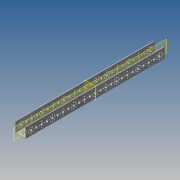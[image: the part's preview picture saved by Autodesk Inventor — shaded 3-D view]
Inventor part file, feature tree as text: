
AUTODESK INVENTOR PART (.ipt)
format: ipt  version: 2020 (Build 240168000, 168)  size: 620,032 bytes
history: native  units: in
note: dims shown in document units (in); Inventor stores cm internally (conversion verified against a paired STEP export)
features: other x216, plane x2, imported_body x1
ambient origin geometry x8: Origin, YZ Plane, XZ Plane, XY Plane, X Axis, Y Axis, Z Axis, Center Point
bodies: Body1 (feature_tree)
feature tree (219):
  other  "tetrix_739069_2012"
  other  "tetrix_739069_20121"
  other  "A_1"
  other  "A_78"
  other  "A_79"
  other  "A_80"
  other  "A_81"
  other  "A_82"
  other  "A_83"
  other  "A_84"
  other  "A_85"
  other  "A_27"
  other  "A_86"
  other  "A_87"
  other  "A_88"
  other  "A_89"
  other  "A_90"
  other  "A_91"
  other  "A_92"
  other  "A_93"
  other  "A_119"
  other  "A_120"
  other  "A_121"
  other  "A_122"
  other  "A_123"
  other  "A_124"
  other  "A_125"
  other  "A_126"
  other  "A_127"
  other  "A_149"
  other  "A_150"
  other  "A_151"
  other  "A_152"
  other  "A_153"
  other  "A_154"
  other  "A_155"
  other  "A_156"
  other  "A_157"
  other  "A_158"
  other  "A_159"
  other  "A_160"
  other  "A_161"
  other  "A_162"
  other  "A_163"
  other  "A_164"
  other  "A_165"
  other  "A_166"
  other  "Work Axis46"
  other  "Work Axis47"
  other  "Work Axis48"
  other  "Work Axis49"
  other  "Work Axis50"
  other  "Work Axis51"
  other  "Work Axis52"
  other  "Work Axis53"
  other  "Work Axis54"
  other  "Work Axis55"
  other  "Work Axis56"
  other  "Work Axis57"
  other  "Work Axis58"
  other  "Work Axis59"
  other  "Work Axis60"
  other  "Work Axis61"
  other  "Work Axis62"
  other  "Work Axis63"
  other  "A_18"
  other  "A_94"
  other  "A_95"
  other  "A_96"
  other  "A_97"
  other  "A_98"
  other  "A_99"
  other  "A_100"
  other  "A_101"
  other  "A_31"
  other  "A_102"
  other  "A_103"
  other  "A_104"
  other  "A_105"
  other  "A_106"
  other  "A_107"
  other  "A_108"
  other  "A_109"
  other  "A_128"
  other  "A_129"
  other  "A_130"
  other  "A_131"
  other  "A_132"
  other  "A_133"
  other  "A_134"
  other  "A_135"
  other  "A_136"
  other  "A_1283"
  other  "A_1284"
  other  "A_1285"
  other  "A_1286"
  other  "A_1287"
  other  "A_1288"
  other  "A_1289"
  other  "A_1290"
  other  "A_1291"
  other  "A_1292"
  other  "A_1293"
  other  "A_1294"
  other  "A_1295"
  other  "A_1296"
  other  "A_1297"
  other  "A_1298"
  other  "A_1299"
  other  "A_1300"
  other  "Work Axis109"
  other  "Work Axis110"
  other  "Work Axis111"
  other  "Work Axis112"
  other  "Work Axis113"
  other  "Work Axis114"
  other  "Work Axis115"
  other  "Work Axis116"
  other  "Work Axis117"
  other  "Work Axis118"
  other  "Work Axis119"
  other  "Work Axis120"
  other  "Work Axis121"
  other  "Work Axis122"
  other  "Work Axis123"
  other  "Work Axis124"
  other  "Work Axis125"
  other  "Work Axis126"
  other  "A_77"
  other  "A_110"
  other  "A_111"
  other  "A_112"
  other  "A_113"
  other  "A_139"
  other  "A_140"
  other  "A_141"
  other  "A_142"
  other  "A_143"
  other  "A_2421"
  other  "A_2422"
  other  "A_2423"
  other  "A_2424"
  other  "A_2425"
  other  "A_2426"
  other  "A_2427"
  other  "A_2428"
  other  "A_2429"
  other  "A_2430"
  other  "A_2449"
  other  "A_2450"
  other  "A_2451"
  other  "A_2452"
  other  "A_2453"
  other  "A_2454"
  other  "A_2455"
  other  "A_2456"
  other  "A_2457"
  other  "A_2458"
  other  "A_114"
  other  "A_115"
  other  "A_116"
  other  "A_117"
  other  "A_118"
  other  "A_144"
  other  "A_145"
  other  "A_146"
  other  "A_147"
  other  "A_148"
  other  "A_2431"
  other  "A_2432"
  other  "A_2433"
  other  "A_2434"
  other  "A_2435"
  other  "A_2436"
  other  "A_2437"
  other  "A_2438"
  other  "A_2439"
  other  "A_2440"
  other  "A_2459"
  other  "A_2460"
  other  "A_2461"
  other  "A_2462"
  other  "A_2463"
  other  "A_2464"
  other  "A_2465"
  other  "A_2466"
  other  "A_2467"
  other  "A_2468"
  other  "A_75"
  other  "A_76"
  other  "A_137"
  other  "A_138"
  other  "A_2441"
  other  "A_2442"
  other  "A_2443"
  other  "A_2444"
  other  "A_2469"
  other  "A_2470"
  other  "A_2471"
  other  "A_2472"
  other  "A_2417"
  other  "A_2418"
  other  "A_2419"
  other  "A_2420"
  other  "A_2445"
  other  "A_2446"
  other  "A_2447"
  other  "A_2448"
  other  "A_2473"
  other  "A_2474"
  other  "A_2475"
  other  "A_2476"
  other  "FRONT"
  other  "TOP"
  other  "RIGHT"
  other  "DTM1"
  plane  "Work Plane5"
  plane  "Work Plane6"
  imported_body  "Base1"
